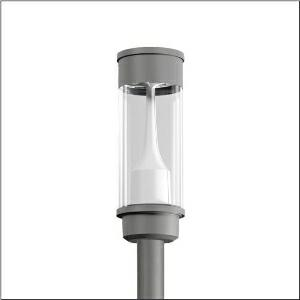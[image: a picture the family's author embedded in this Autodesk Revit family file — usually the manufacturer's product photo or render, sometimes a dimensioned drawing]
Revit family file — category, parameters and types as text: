
# Revit family: litepole_iq___p1_0a_5xa5415nf14hp_9138
name_source: partatom
category: Lighting Fixtures
units: mm (PartAtom-declared; Revit-internal decimal feet)

## family parameters
Cut with Voids When Loaded = No
Host = Face
Light Source = No
Part Type = Normal
Room Calculation Point = No
Round Connector Dimension = Use Diameter
Shared = No

## types (1)
- --- (1 x LED, 4210 lm, 33.6 W, 2700K)
    Apparent Load = 34 VA
    CIE Flux Codes = 31 60 90 94 100
    Color Rendering = 70
    Color Temperature = 2700K
    Default Elevation = 1800 mm
    Description = Litepole iQ, mast luminaire, Module 540 iQ-SR, primary light control with 3 zone facetted reflector, of plastic, silver coated, highly specular, structured, primary optical cover: cover, of PMMA, transparent, partly coated, light distribution: P1.0a, light emission: direct distribution, primary light characteristic: strongly asymmetric, installation type: post-top, LED, High Power LED, rated luminous flux: 4.210lm, luminous efficacy: 125lm/W, light colour: 727, colour temperature: 2700K, control gear: iQ Street-Remote, control: optimised constant luminous flux control (CLO 2.0), Desk-Remote (wireless, voltage-free reading and setting of iQ features in the workshop via application-optimized NFC function/RFID function), Light-Fading, Smart-Wire, Night-Set, Lumen-Switch, Temp-Guard, Auto-Match, Street-Remote, pre-setting: logarithmic dimming characteristic, with terminal, 6-pole, max. 2.5mm², mains connection: 230..240V, AC, 50/60Hz, start of lifetime: 34W, end of service life: 36W, reduction: 15W, luminaire housing, upper part, of glass-fibre reinforced polyester, coated, Siteco® metallic grey (DB 702S), diameter: 210mm, height: 590mm, spigot size: d x l = 76 x 70mm (post-top) | with reducer (optional accessory) 60 x 70mm, mounting height: 3..5m, post-top mast mounting element, of diecast aluminium, coated, Siteco® metallic grey (DB 702S), Module 540 iQ-SR, traffic white (RAL 9016), equipment: Power, protection rating (complete): IP65, insulation class (complete): insulation class II (safety insulation), certification: CE, ENEC, VDE, packaging unit: 1 piece

Light Distribution: P1.0a
    Height = 590 mm
    Lamp = 1 x LED
    Lamp Light Flux = 4210 lm
    Lamp Power = 33.6 W
    Lamp count = 1
    Length = 220 mm
    Luminous efficacy = 125 lm/W
    Manufacturer = Siteco
    ModVariant = No
    Model = 5XA5415NF14HP
    Number of Poles = 1
    OnlyDefault = Yes
    Power Factor = 1
    Product Name = Litepole iQ | P1.0a
    Product group = mast luminaire | pylon top
    ProductGroupID = 6100
    Protection Class = Protection class II
    Protection Degree = IP 65
    RLX_Detail_Level = 1
    RLX_Emergency_Light_Flux = 0 lm
    RLX_Emergency_Type = 0
    RLX_Emergency_Type_DB = No
    RlxData = <blob elided: 29937 chars, md5=ded436b9>
    Socket = socket
    Standby Power = 0 W
    System Light Flux = 4210 lm
    System Power = 34 W
    Type Comments = factory setting: luminous flux: 100 % | dim-lin: 254 | 695 mA
    Type Image = l_1006025.jpg
    URL = http://relux.com
    VarID = @adj_174395
    Voltage = 0 V
    Weight = 0.00 kg
    Width = 0 mm  [stored 0 ft]

note: [stored X ft] marks values corroborated as IEEE doubles in the binary element streams (Revit-internal decimal feet)

## geometry (parser evidence)
native form markers: Blend x4, Sweep x12
no freeform markers — native parametric forms only
